# Revit family: Intercept
name_source: partatom
category: Lighting Fixtures
units: mm (PartAtom-declared; Revit-internal decimal feet)

## family parameters
Cut with Voids When Loaded = No
Host = Face
Light Source = Yes
OmniClass Number = 23.80.70.11.14.21
OmniClass Title = Spots and Tracklight Specialties
Part Type = Normal
Room Calculation Point = No
Round Connector Dimension = Use Diameter
Shared = Yes

## types (1)
- Intercept
    Apparent Load = 0 VA
    Assembly Code = D5020230
    Color Filter = 16777215
    Control Options = Continuious Dimming/ SiteSync pre-comm/NX Fixture Module/DMX/RDM
    Default Elevation = 48 "
    Description = Superior high output, high efficiency LED floodlight with a variety of flood distributions
    Dimming Lamp Color Temperature Shift = <None>
    Distribution = 2X2,3X3,4X4,5X5
    Front Housing Material = Paint - Textured Camera Black
    Housing Material = Paint - Light Silver
    Lamp = LED
    Light Source Symbol Length = 120 "
    Load Classification = Lighting
    Manufacturer = EXO
    Model = Intercept
    Mounting = Yoke/ Under Mount yoke
    Photometric Notes = More IES files download on Photometric Link
    Power Factor = 1
    Spot Beam Angle = 30.00°
    Spot Field Angle = 90.00°
    Tilt Angle = 0.00°
    Type Comments = Lighting Fixture
    URL = https://www.currentlighting.com
    Voltage = 120 V
    Warranty = 5-Years Warranty
    Wattage Comments = 440W,580W,880W

## geometry (parser evidence)
native form markers: Sweep x2
no freeform markers — native parametric forms only
